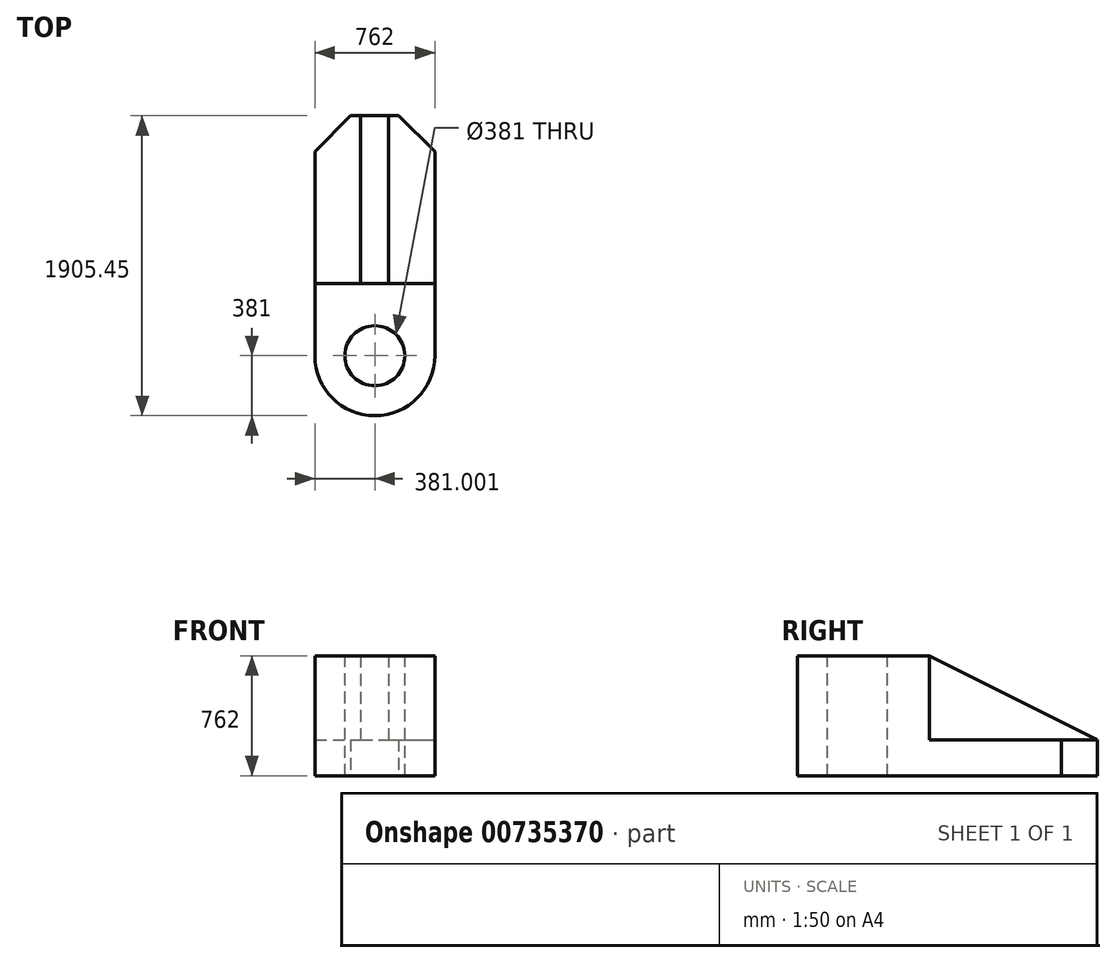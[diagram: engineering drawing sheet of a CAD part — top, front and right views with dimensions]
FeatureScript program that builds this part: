
annotation { "Feature Type Name" : "Feature", "Feature Type Description" : "" }
export const myFeature = defineFeature(function(context is Context, id is Id, definition is map)
    precondition{}
    {
        {
            var Q0;
            Q0=qCreatedBy(makeId("Top.planeOp"),FACE);
            var sketch = newSketch(context, id + "F0", { "sketchPlane" : qUnion([Q0])});
            skLineSegment(sketch, "E0", {"start": v(-281.25, 444.1) * mm, "end": v(23.55, 444.1) * mm});
            skLineSegment(sketch, "E1", {"start": v(23.55, 444.1) * mm, "end": v(253.36, 215.5) * mm});
            skLineSegment(sketch, "E2", {"start": v(253.36, 215.5) * mm, "end": v(253.36, -1079.9) * mm});
            skLineSegment(sketch, "E3", {"start": v(253.36, -1079.9) * mm, "end": v(-508.64, -1079.9) * mm});
            skLineSegment(sketch, "E4", {"start": v(-508.64, -1079.9) * mm, "end": v(-508.64, 215.5) * mm});
            skLineSegment(sketch, "E5", {"start": v(-508.64, 215.5) * mm, "end": v(-281.25, 444.1) * mm});
            skSolve(sketch);
        }
        {
            var Q0;
            Q0=qCreatedBy(makeId("Top.planeOp"),FACE);
            var sketch = newSketch(context, id + "F1", { "sketchPlane" : qUnion([Q0])});
            skCircle(sketch, "E6", {"center": v(-127.64, -1080.36) * mm, "radius": 381 * mm});
            skLineSegment(sketch, "E7.bottom", {"start": v(253.36, -623.16) * mm, "end": v(-508.64, -623.16) * mm});
            skLineSegment(sketch, "E7.top", {"start": v(253.36, -1080.36) * mm, "end": v(-508.64, -1080.36) * mm});
            skLineSegment(sketch, "E7.left", {"start": v(253.36, -623.16) * mm, "end": v(253.36, -1080.36) * mm});
            skLineSegment(sketch, "E7.right", {"start": v(-508.64, -623.16) * mm, "end": v(-508.64, -1080.36) * mm});
            skSolve(sketch);
        }
        {
            var Q0;
            Q0=makeQuery(id+"F0.imprint","IMPRINT",FACE,{"disambiguationData":[TD([[makeQuery(id+"F0.imprint","IMPRINT",EDGE,{"derivedFrom":sQuery(id+"F0.wireOp",EDGE,"E0")}),-1.0]])]});
            extrude(context, id + "F2", {"entities" : qUnion([Q0]), "depth" : 228.6 * mm, "offsetDistance" : 25.4 * mm});
        }
        {
            var Q0;
            Q0 = qSketchRegion(id + "F1", true);
            extrude(context, id + "F3", {"entities" : qUnion([Q0]), "operationType" : NewBodyOperationType.ADD, "depth" : 762 * mm, "offsetDistance" : 25.4 * mm});
        }
        {
            var Q0;
            Q0=makeQuery(id+"F2.opExtrude","CAP_FACE",FACE,{"disambiguationData":[OSD([sQuery(id+"F0.wireOp",EDGE,"E0"),sQuery(id+"F0.wireOp",EDGE,"E1"),sQuery(id+"F0.wireOp",EDGE,"E2"),sQuery(id+"F0.wireOp",EDGE,"E3"),sQuery(id+"F0.wireOp",EDGE,"E4"),sQuery(id+"F0.wireOp",EDGE,"E5")])],"isStart":false});
            var sketch = newSketch(context, id + "F4", { "sketchPlane" : qUnion([Q0])});
            skLineSegment(sketch, "E8.bottom", {"start": v(-217.75, 444.1) * mm, "end": v(-39.95, 444.1) * mm});
            skLineSegment(sketch, "E8.top", {"start": v(-217.75, -623.16) * mm, "end": v(-39.95, -623.16) * mm});
            skLineSegment(sketch, "E8.left", {"start": v(-217.75, 444.1) * mm, "end": v(-217.75, -623.16) * mm});
            skLineSegment(sketch, "E8.right", {"start": v(-39.95, 444.1) * mm, "end": v(-39.95, -623.16) * mm});
            skSolve(sketch);
        }
        {
            var Q0;
            Q0=makeQuery(id+"F4.imprint","IMPRINT",FACE,{"disambiguationData":[TD([[makeQuery(id+"F4.imprint","IMPRINT",EDGE,{"derivedFrom":sQuery(id+"F4.wireOp",EDGE,"E8.bottom")}),-1.0]])]});
            extrude(context, id + "F5", {"entities" : qUnion([Q0]), "operationType" : NewBodyOperationType.ADD, "depth" : 533.4 * mm, "offsetDistance" : 25.4 * mm});
        }
        {
            var Q0;
            Q0=makeQuery(id+"F5.opExtrude","SWEPT_FACE",FACE,{"disambiguationData":[OSD([sQuery(id+"F4.wireOp",EDGE,"E8.right")])]});
            var sketch = newSketch(context, id + "F6", { "sketchPlane" : qUnion([Q0])});
            skLineSegment(sketch, "E9", {"start": v(-623.16, 762) * mm, "end": v(444.1, 228.6) * mm});
            skLineSegment(sketch, "E10", {"start": v(-623.16, 762) * mm, "end": v(444.1, 762) * mm});
            skLineSegment(sketch, "E11", {"start": v(444.1, 762) * mm, "end": v(444.1, 228.6) * mm});
            skSolve(sketch);
        }
        {
            var Q0;
            Q0=makeQuery(id+"F6.imprint","IMPRINT",FACE,{"disambiguationData":[TD([[makeQuery(id+"F6.imprint","IMPRINT",EDGE,{"derivedFrom":sQuery(id+"F6.wireOp",EDGE,"E9")}),1.0]])]});
            extrude(context, id + "F7", {"entities" : qUnion([Q0]), "operationType" : NewBodyOperationType.REMOVE, "oppositeDirection" : true, "depth" : 3810 * mm, "offsetDistance" : 25.4 * mm});
        }
        {
            var Q0;
            Q0=makeQuery(id+"F5.boolean.opBoolean","MERGE",FACE,{"derivedFrom":[makeQuery(id+"F3.opExtrude","CAP_FACE",FACE,{"disambiguationData":[OSD([sQuery(id+"F1.wireOp",EDGE,"E6"),sQuery(id+"F1.wireOp",EDGE,"E7.bottom"),sQuery(id+"F1.wireOp",EDGE,"E7.left"),sQuery(id+"F1.wireOp",EDGE,"E7.right")])],"isStart":false}),makeQuery(id+"F5.opExtrude","CAP_FACE",FACE,{"disambiguationData":[OSD([sQuery(id+"F4.wireOp",EDGE,"E8.bottom"),sQuery(id+"F4.wireOp",EDGE,"E8.top"),sQuery(id+"F4.wireOp",EDGE,"E8.left"),sQuery(id+"F4.wireOp",EDGE,"E8.right")])],"isStart":false})]});
            var sketch = newSketch(context, id + "F8", { "sketchPlane" : qUnion([Q0])});
            skCircle(sketch, "E12", {"center": v(-127.64, -1080.36) * mm, "radius": 190.5 * mm});
            skSolve(sketch);
        }
        {
            var Q0;
            Q0=makeQuery(id+"F8.imprint","IMPRINT",FACE,{"disambiguationData":[TD([[makeQuery(id+"F8.imprint","IMPRINT",EDGE,{"derivedFrom":sQuery(id+"F8.wireOp",EDGE,"E12")}),1.0]])]});
            extrude(context, id + "F9", {"entities" : qUnion([Q0]), "operationType" : NewBodyOperationType.REMOVE, "oppositeDirection" : true, "depth" : 1143 * mm, "offsetDistance" : 25.4 * mm});
        }
    });
